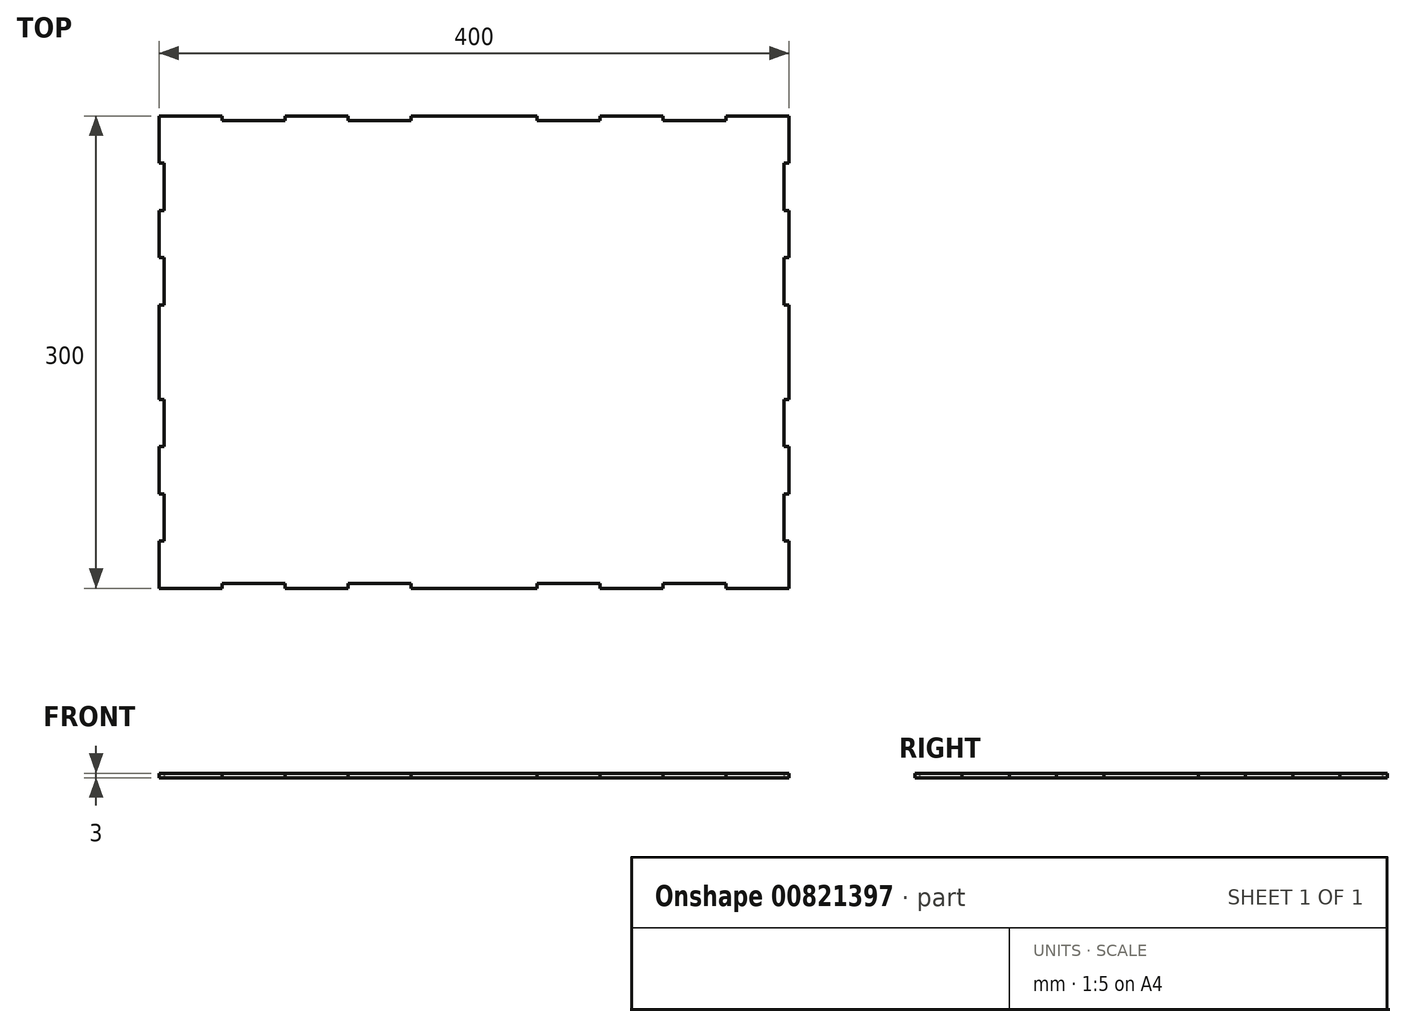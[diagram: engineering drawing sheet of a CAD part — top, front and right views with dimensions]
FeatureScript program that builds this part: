
annotation { "Feature Type Name" : "Feature", "Feature Type Description" : "" }
export const myFeature = defineFeature(function(context is Context, id is Id, definition is map)
    precondition{}
    {
        {
            var Q0;
            Q0=qCreatedBy(makeId("Top.planeOp"),FACE);
            var sketch = newSketch(context, id + "F0", { "sketchPlane" : qUnion([Q0])});
            skPoint(sketch, "E0.middle", {"position": v(0, 0) * mm});
            skLineSegment(sketch, "E1.bottom", {"start": v(-160, -150) * mm, "end": v(-200, -150) * mm});
            skLineSegment(sketch, "E1.left", {"start": v(-160, -150) * mm, "end": v(-160, -147) * mm});
            skPoint(sketch, "E1.middle", {"position": v(-180, -148.5) * mm});
            skLineSegment(sketch, "E2.top", {"start": v(-40, -147) * mm, "end": v(-80, -147) * mm});
            skLineSegment(sketch, "E2.left", {"start": v(-40, -150) * mm, "end": v(-40, -147) * mm});
            skLineSegment(sketch, "E2.right", {"start": v(-80, -150) * mm, "end": v(-80, -147) * mm});
            skPoint(sketch, "E2.middle", {"position": v(-60, -148.5) * mm});
            skLineSegment(sketch, "E3.bottom", {"start": v(-80, -150) * mm, "end": v(-120, -150) * mm});
            skLineSegment(sketch, "E3.right", {"start": v(-120, -150) * mm, "end": v(-120, -147) * mm});
            skPoint(sketch, "E3.middle", {"position": v(-100, -148.5) * mm});
            skPoint(sketch, "E4.middle", {"position": v(-20, -148.5) * mm});
            skLineSegment(sketch, "E5.top", {"start": v(-120, -147) * mm, "end": v(-160, -147) * mm});
            skPoint(sketch, "E5.middle", {"position": v(-140, -148.5) * mm});
            skLineSegment(sketch, "E6.MirrorCS", {"start": v(40, -150) * mm, "end": v(40, -147) * mm});
            skLineSegment(sketch, "E7.MirrorCS", {"start": v(80, -150) * mm, "end": v(80, -147) * mm});
            skLineSegment(sketch, "E8.MirrorCS", {"start": v(160, -150) * mm, "end": v(160, -147) * mm});
            skLineSegment(sketch, "E9.MirrorCS", {"start": v(120, -150) * mm, "end": v(120, -147) * mm});
            skPoint(sketch, "E10.MirrorP", {"position": v(20, -148.5) * mm});
            skLineSegment(sketch, "E11.MirrorCS", {"start": v(80, -150) * mm, "end": v(120, -150) * mm});
            skLineSegment(sketch, "E12.MirrorCS", {"start": v(120, -147) * mm, "end": v(160, -147) * mm});
            skPoint(sketch, "E13.MirrorP", {"position": v(100, -148.5) * mm});
            skLineSegment(sketch, "E14.MirrorCS", {"start": v(160, -150) * mm, "end": v(200, -150) * mm});
            skLineSegment(sketch, "E15.MirrorCS", {"start": v(40, -147) * mm, "end": v(80, -147) * mm});
            skPoint(sketch, "E16.MirrorP", {"position": v(60, -148.5) * mm});
            skPoint(sketch, "E17.MirrorP", {"position": v(180, -148.5) * mm});
            skPoint(sketch, "E18.MirrorP", {"position": v(140, -148.5) * mm});
            skLineSegment(sketch, "E19.MirrorCS", {"start": v(-160, 150) * mm, "end": v(-160, 147) * mm});
            skLineSegment(sketch, "E20.MirrorCS", {"start": v(-80, 150) * mm, "end": v(-80, 147) * mm});
            skLineSegment(sketch, "E21.MirrorCS", {"start": v(120, 150) * mm, "end": v(120, 147) * mm});
            skLineSegment(sketch, "E22.MirrorCS", {"start": v(40, 150) * mm, "end": v(40, 147) * mm});
            skLineSegment(sketch, "E23.MirrorCS", {"start": v(-120, 150) * mm, "end": v(-120, 147) * mm});
            skLineSegment(sketch, "E24.MirrorCS", {"start": v(160, 150) * mm, "end": v(160, 147) * mm});
            skLineSegment(sketch, "E25.MirrorCS", {"start": v(80, 150) * mm, "end": v(80, 147) * mm});
            skLineSegment(sketch, "E26.MirrorCS", {"start": v(-40, 150) * mm, "end": v(-40, 147) * mm});
            skPoint(sketch, "E27.MirrorP", {"position": v(140, 148.5) * mm});
            skPoint(sketch, "E28.MirrorP", {"position": v(-140, 148.5) * mm});
            skPoint(sketch, "E29.MirrorP", {"position": v(-100, 148.5) * mm});
            skLineSegment(sketch, "E30.MirrorCS", {"start": v(-160, 150) * mm, "end": v(-200, 150) * mm});
            skPoint(sketch, "E31.MirrorP", {"position": v(180, 148.5) * mm});
            skPoint(sketch, "E32.MirrorP", {"position": v(60, 148.5) * mm});
            skPoint(sketch, "E33.MirrorP", {"position": v(-20, 148.5) * mm});
            skLineSegment(sketch, "E34.MirrorCS", {"start": v(160, 150) * mm, "end": v(200, 150) * mm});
            skPoint(sketch, "E35.MirrorP", {"position": v(-180, 148.5) * mm});
            skLineSegment(sketch, "E36.MirrorCS", {"start": v(120, 147) * mm, "end": v(160, 147) * mm});
            skLineSegment(sketch, "E37.MirrorCS", {"start": v(80, 150) * mm, "end": v(120, 150) * mm});
            skPoint(sketch, "E38.MirrorP", {"position": v(20, 148.5) * mm});
            skLineSegment(sketch, "E39.MirrorCS", {"start": v(-80, 150) * mm, "end": v(-120, 150) * mm});
            skLineSegment(sketch, "E40.MirrorCS", {"start": v(-120, 147) * mm, "end": v(-160, 147) * mm});
            skPoint(sketch, "E41.MirrorP", {"position": v(100, 148.5) * mm});
            skLineSegment(sketch, "E42.MirrorCS", {"start": v(-40, 147) * mm, "end": v(-80, 147) * mm});
            skPoint(sketch, "E43.MirrorP", {"position": v(-60, 148.5) * mm});
            skLineSegment(sketch, "E44.MirrorCS", {"start": v(40, 147) * mm, "end": v(80, 147) * mm});
            skLineSegment(sketch, "E45", {"start": v(-40, -150) * mm, "end": v(40, -150) * mm});
            skLineSegment(sketch, "E46", {"start": v(-40, 150) * mm, "end": v(40, 150) * mm});
            skLineSegment(sketch, "E47.top", {"start": v(-197, -120) * mm, "end": v(-200, -120) * mm});
            skLineSegment(sketch, "E47.right", {"start": v(-200, -150) * mm, "end": v(-200, -120) * mm});
            skPoint(sketch, "E47.middle", {"position": v(-198.5, -135) * mm});
            skLineSegment(sketch, "E48.top", {"start": v(-197, -90) * mm, "end": v(-200, -90) * mm});
            skLineSegment(sketch, "E48.left", {"start": v(-197, -120) * mm, "end": v(-197, -90) * mm});
            skPoint(sketch, "E48.middle", {"position": v(-198.5, -105) * mm});
            skLineSegment(sketch, "E49.top", {"start": v(-197, -60) * mm, "end": v(-200, -60) * mm});
            skLineSegment(sketch, "E49.right", {"start": v(-200, -90) * mm, "end": v(-200, -60) * mm});
            skPoint(sketch, "E49.middle", {"position": v(-198.5, -75) * mm});
            skLineSegment(sketch, "E50.top", {"start": v(-197, -30) * mm, "end": v(-200, -30) * mm});
            skLineSegment(sketch, "E50.left", {"start": v(-197, -60) * mm, "end": v(-197, -30) * mm});
            skPoint(sketch, "E50.middle", {"position": v(-198.5, -45) * mm});
            skPoint(sketch, "E51.endSnap0", {"position": v(-198.5, -90) * mm});
            skPoint(sketch, "E52.middle", {"position": v(-198.5, -15) * mm});
            skLineSegment(sketch, "E53.MirrorCS", {"start": v(-197, 90) * mm, "end": v(-200, 90) * mm});
            skLineSegment(sketch, "E54.MirrorCS", {"start": v(-197, 120) * mm, "end": v(-200, 120) * mm});
            skLineSegment(sketch, "E55.MirrorCS", {"start": v(-197, 60) * mm, "end": v(-200, 60) * mm});
            skLineSegment(sketch, "E56.MirrorCS", {"start": v(-197, 30) * mm, "end": v(-200, 30) * mm});
            skPoint(sketch, "E57.MirrorP", {"position": v(-198.5, 105) * mm});
            skLineSegment(sketch, "E58.MirrorCS", {"start": v(-197, 60) * mm, "end": v(-197, 30) * mm});
            skLineSegment(sketch, "E59.MirrorCS", {"start": v(-200, 90) * mm, "end": v(-200, 60) * mm});
            skLineSegment(sketch, "E60.MirrorCS", {"start": v(-197, 120) * mm, "end": v(-197, 90) * mm});
            skLineSegment(sketch, "E61.MirrorCS", {"start": v(-200, 150) * mm, "end": v(-200, 120) * mm});
            skPoint(sketch, "E62.MirrorP", {"position": v(-198.5, 15) * mm});
            skPoint(sketch, "E63.MirrorP", {"position": v(-198.5, 135) * mm});
            skPoint(sketch, "E64.MirrorP", {"position": v(-198.5, 90) * mm});
            skPoint(sketch, "E65.MirrorP", {"position": v(-198.5, 75) * mm});
            skPoint(sketch, "E66.MirrorP", {"position": v(-198.5, 45) * mm});
            skLineSegment(sketch, "E67", {"start": v(-200, 30) * mm, "end": v(-200, -30) * mm});
            skLineSegment(sketch, "E68.MirrorCS", {"start": v(197, -90) * mm, "end": v(200, -90) * mm});
            skLineSegment(sketch, "E69.MirrorCS", {"start": v(197, 90) * mm, "end": v(200, 90) * mm});
            skLineSegment(sketch, "E70.MirrorCS", {"start": v(197, 60) * mm, "end": v(200, 60) * mm});
            skLineSegment(sketch, "E71.MirrorCS", {"start": v(197, 120) * mm, "end": v(200, 120) * mm});
            skLineSegment(sketch, "E72.MirrorCS", {"start": v(197, 30) * mm, "end": v(200, 30) * mm});
            skLineSegment(sketch, "E73.MirrorCS", {"start": v(197, -60) * mm, "end": v(200, -60) * mm});
            skLineSegment(sketch, "E74.MirrorCS", {"start": v(197, -30) * mm, "end": v(200, -30) * mm});
            skLineSegment(sketch, "E75.MirrorCS", {"start": v(197, -120) * mm, "end": v(200, -120) * mm});
            skLineSegment(sketch, "E76.MirrorCS", {"start": v(200, -90) * mm, "end": v(200, -60) * mm});
            skLineSegment(sketch, "E77.MirrorCS", {"start": v(200, 90) * mm, "end": v(200, 60) * mm});
            skPoint(sketch, "E78.MirrorP", {"position": v(198.5, -75) * mm});
            skLineSegment(sketch, "E79.MirrorCS", {"start": v(197, 60) * mm, "end": v(197, 30) * mm});
            skPoint(sketch, "E80.MirrorP", {"position": v(198.5, -90) * mm});
            skPoint(sketch, "E81.MirrorP", {"position": v(198.5, 45) * mm});
            skPoint(sketch, "E82.MirrorP", {"position": v(198.5, 75) * mm});
            skPoint(sketch, "E83.MirrorP", {"position": v(198.5, 105) * mm});
            skPoint(sketch, "E84.MirrorP", {"position": v(198.5, -15) * mm});
            skPoint(sketch, "E85.MirrorP", {"position": v(198.5, 135) * mm});
            skLineSegment(sketch, "E86.MirrorCS", {"start": v(200, 150) * mm, "end": v(200, 120) * mm});
            skLineSegment(sketch, "E87.MirrorCS", {"start": v(197, -120) * mm, "end": v(197, -90) * mm});
            skLineSegment(sketch, "E88.MirrorCS", {"start": v(200, -150) * mm, "end": v(200, -120) * mm});
            skPoint(sketch, "E89.MirrorP", {"position": v(198.5, 15) * mm});
            skPoint(sketch, "E90.MirrorP", {"position": v(198.5, 90) * mm});
            skPoint(sketch, "E91.MirrorP", {"position": v(198.5, -135) * mm});
            skPoint(sketch, "E92.MirrorP", {"position": v(198.5, -105) * mm});
            skLineSegment(sketch, "E93.MirrorCS", {"start": v(197, 120) * mm, "end": v(197, 90) * mm});
            skLineSegment(sketch, "E94.MirrorCS", {"start": v(197, -60) * mm, "end": v(197, -30) * mm});
            skLineSegment(sketch, "E95.MirrorCS", {"start": v(200, 30) * mm, "end": v(200, -30) * mm});
            skPoint(sketch, "E96.MirrorP", {"position": v(198.5, -45) * mm});
            skSolve(sketch);
        }
        {
            var Q0;
            Q0=makeQuery(id+"F0.imprint","IMPRINT",FACE,{"disambiguationData":[TD([[makeQuery(id+"F0.imprint","IMPRINT",EDGE,{"derivedFrom":sQuery(id+"F0.wireOp",EDGE,"E2.top")}),-1.0]])]});
            extrude(context, id + "F1", {"entities" : qUnion([Q0]), "depth" : 3 * mm, "offsetDistance" : 25 * mm});
        }
    });
